# Revit family: IS_iLifeA_T4522_BIM_NL
name_source: partatom
category: Plumbing Fixtures
units: mm (PartAtom-declared; Revit-internal decimal feet)

## family parameters
Always vertical = No
Cut with Voids When Loaded = No
OmniClass Number = 23.45.05.21.11.11
OmniClass Title = Water Operated Water Closets
Part Type = Normal
Room Calculation Point = No
Round Connector Dimension = Use Diameter
Shared = No
Work Plane-Based = No

## types (2) — shared parameters
Accesoires = https://www.idealstandard.nl
Accessories = https://www.idealstandard.nl
Afmetingen = 540 x 340 x 360mm
AfstandsEenheid = millimeter
AreaMeasurement = internal
AreaUnits = Millimeter
Artikelreferentie = I.life Eine wandhängende Schüssel mit offener Befestigung
Auteur = Ideal Standard
BIMObjectName = IS_IdealStandard_WCpans_I.life_T4522
BIMobject category = Toilets
BIMobject category code = sanitary-toilets
BIMobject main category = Sanitary
BIMobject main category code = sanitary
Beschrijvinggarantie = Herstellergarantie
BimObjectNaam = IS_IdealStandard_WCpans_I.life_T4522
Brand = Ideal Standard
Brand url = http://https:
ConnectionType = Plumbing
CurrencyUnit = €
CurrentRevision = 1
Date of publishing = 28/06/2021
DurationUnit = Years
DuurEenheid = Jaar
Edition number = 1
Eigenschappen = Offene Befestigung der wandhängenden WC-Schüssel
Features = Wall-Hung WC Bowl open fixation
Garantieonderdelen = 5
Garantieunits = Jaar
GemaaktOp = 40722
Help = https://www.idealstandard.nl
Hoogte = 340.042259216309
Hulp = https://www.idealstandard.nl
IFC Classification = Sanitary Terminal
IfcExportAs = IfcSanitaryTerminalType
IfcExportType = TOILETPAN
Installatieinstructies = https://www.idealstandard.nl
Installation instructions = https://www.idealstandard.nl
InstallationInstructions = https://www.idealstandard.nl
Lengte = 540 mm
LinearUnits = millimeter
MaintenanceInformation = https://www.idealstandard.nl
Manufacturer = Ideal Standard
Manufacturer name = Ideal Standard
ManufacturerURL = https://www.idealstandard.nl
Masterformat 2014 Code = 12 46 16
Masterformat 2014 Description = Bowls
Materiaal = Vitrous China
MateriaalWC = Vitrous China
Material = Vitrous China
Material main = Vitrous China
Merk = Ideal Standard
ModelReference = I.life A wallhung bowl open fixation
Montageinstuctie = https://www.idealstandard.nl
NBS Reference Code = 45-35-70/384
NBS Reference Description = WC pans
Name = WCpans_I.life_T4522_IdealStandard
NettWeight = 18
Nettogewicht = 18
NominalDepth = 540 mm
NominalHeight = 340 mm
NominalWidth = 360 mm
Normen = WCpans_I.life_T4522_IdealStandard
OmniClass Code = 23-31 19 00
OmniClass Description = Toilets
OppervlakteEenheid = Millimeter
PanMaterial = Vitrous China
PanMounting = Wallhung
Product Guid = 05ede8fa-1680-485b-9e6f-e66815405710
Product SKU = T4522
Product certification = https://www.idealstandard.nl
Product data url = https://bimobject.com
Product family = I.life
Product group = Bowl
Product name = I.life A wallhung bowl open fixation
Product url = https://www.idealstandard.nl
ProductInformation = https://www.idealstandard.nl
ProductSoort = WC-Schüssel
Productinformatie = https://www.idealstandard.nl
QR code = http://bimobject.com
Referentie = I.life Eine wandhängende Schüssel mit offener Befestigung
Revisie = 1
Shape = sculpture
Size = 540 x 340 x 360mm
Space = Internal
SpareParts = https://www.idealstandard.nl
Technical description = https://www.idealstandard.nl
Telefoonnummer = 077 355 08 08
ToiletPanType = wallhung bowl
ToiletType = wallhung bowl
TypeWC = wallhung bowl
Typeconnectie = Installation
TypespoelingWC = abwaschen spülen
UNSPSC Code = 30181511
URL = https://https:
Uniclass 1.4 Code = L7216
Uniclass 1.4 Description = Toilets
Uniclass 2.0 Code = PR-35-93-94
Uniclass 2.0 Description = Wc Pans
Uniclass 2015 Code = Pr_40_20_93_94
Uniclass 2015 Name = WC pans
Uniclass2015Beschrijving = WC pans
Uniclass2015Code = Pr_40_20_93_94
Uniclass2015Referentie = Pr_40_20_93_94
Uniclass2015Title = WC pans
Uniclass2015Version = v1.20
Urlproducent = https://https:
ValutaEenheid = €
Versie = 1
Version = 1
VolumeUnits = Liter
Volumeunits = Liter
Vorm = beeldhouwwerk
WRASURL = https://www.wrasapprovals.co.uk
WarrantyDescription = manufacturer warranty
WarrantyDurationParts = 99
WarrantyDurationUnit = years
Wisselstukken = https://www.idealstandard.nl
Youtube clip = https://www.youtube.com
zero-valued in all types: Breedte, BrutoGewicht, Cost, Diepte, DrainSize, GrootteAfvoergat, Overloop, Vervangingskosten

## per-type parameters (varying)
| type | Afwerking | Artikelnummer | Artikelomschrijving | BarCode | Barcode | Color | Description | Finish | GTIN code | Kleur | Kleurwc | MainColor | Model | ModelNumber | PanColor |
| T4522MA - I.life A wallhung bowl open fixation - Ideal Plus White | IdealPlusWeiß | T4522MA | I.life A wandhängende Schüssel offene Befestigung - Ideal Plus Weiß | 8014140486749 | 8014140486749 | IdealPlusWeiß | I.life A wandhängende Schüssel offene Befestigung - Ideal Plus Weiß | IdealPlusWeiß | https://8014140486749 | IdealPlusWeiß | IdealPlusWeiß | IdealPlusWhite | T4522MA | T4522MA | Ideal Plus White |
| T452201 - I.life A wallhung bowl open fixation - White | Weiß | T452201 | I.life A wandhängende Schüssel offene Befestigung - Weiß | 8014140485902 | 8014140485902 | Weiß | I.life A wandhängende Schüssel offene Befestigung - Weiß | Weiß | https://8014140485902 | Weiß | Weiß | White | T452201 | T452201 | White |

## geometry (parser evidence)
native form markers: Sweep x3
no freeform markers — native parametric forms only
